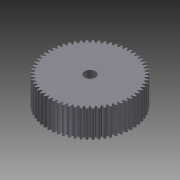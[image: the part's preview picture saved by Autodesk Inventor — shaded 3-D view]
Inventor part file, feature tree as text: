
AUTODESK INVENTOR PART (.ipt)
format: ipt  version: 2011 (Build 150239000, 239)  size: 352,768 bytes
history: native  units: mm (DEFAULTED — no unit token found)
features: plane x3, other x3, sketch x2, extrude x1, hole x1
ambient origin geometry x8: Origin, YZ Plane, XZ Plane, XY Plane, X Axis, Y Axis, Z Axis, Center Point
bodies: Solid1 (feature_tree)
feature tree (10):
  extrude  "Extrusion1"  Depth=5.0mm TaperAngle=0.0deg
  plane  "Work Plane2"
  plane  "Work Plane8"
  plane  "Work Plane9"
  other  "Spur Gear"
  hole  "Hole1"  [1 undecoded]
  sketch  "Sketch1"  dims[d0=15.5mm d1=5.0mm d2=0.0mm]
  sketch  "Sketch2"  dims[d3=15.0mm d4=10.0mm d5=0.0mm d16=10.0mm d17=0.0mm d34=0.523599mm d39=0.0mm d41=0.0mm d43=10.0mm d46=10.0mm d47=0.0mm d48=0.0mm d49=10.0mm d50=10.0mm d51=2.0mm d52=6.0mm d53=4.0mm d54=2.0mm d55=90.0deg d56=8.0mm d57=20.594885mm]
  other  "Srf1"
  other  "Pitch Diameter"
note: 1 required parameter value undecoded (feature->parameter linkage not recoverable at this tier; creation-order binding heuristic only, values carry confidence <= 0.55)
